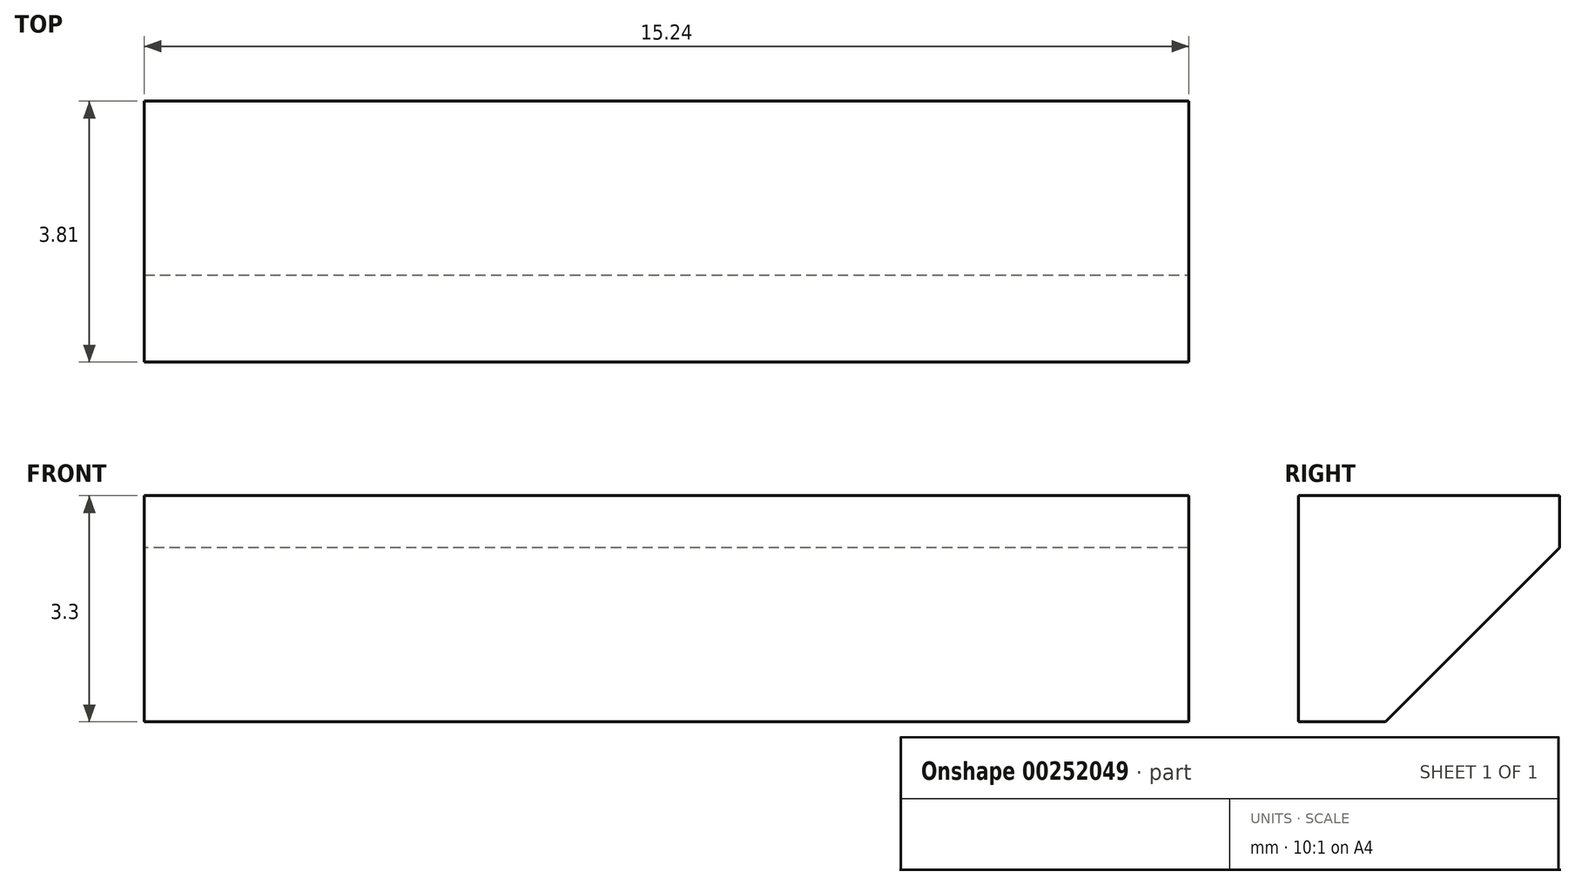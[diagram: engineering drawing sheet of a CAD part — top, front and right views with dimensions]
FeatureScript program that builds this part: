
annotation { "Feature Type Name" : "Feature", "Feature Type Description" : "" }
export const myFeature = defineFeature(function(context is Context, id is Id, definition is map)
    precondition{}
    {
        {
            var Q0;
            Q0=qCreatedBy(makeId("Front.planeOp"),FACE);
            var sketch = newSketch(context, id + "F0", { "sketchPlane" : qUnion([Q0])});
            skLineSegment(sketch, "E0.bottom", {"start": v(-7.62, 1.65) * mm, "end": v(7.62, 1.65) * mm});
            skLineSegment(sketch, "E0.top", {"start": v(-7.62, -1.65) * mm, "end": v(7.62, -1.65) * mm});
            skLineSegment(sketch, "E0.left", {"start": v(-7.62, 1.65) * mm, "end": v(-7.62, -1.65) * mm});
            skLineSegment(sketch, "E0.right", {"start": v(7.62, 1.65) * mm, "end": v(7.62, -1.65) * mm});
            skPoint(sketch, "E0.middle", {"position": v(0, 0) * mm});
            skSolve(sketch);
        }
        {
            var Q0;
            Q0 = qSketchRegion(id + "F0", true);
            extrude(context, id + "F1", {"entities" : qUnion([Q0]), "depth" : 3.8 * mm});
        }
        {
            var Q0;
            Q0=makeQuery(id+"F1.opExtrude","CAP_EDGE",EDGE,{"disambiguationData":[OSD([sQuery(id+"F0.wireOp",EDGE,"E0.top")])],"isStart":true});
            chamfer(context, id + "F2", {"entities" : qUnion([Q0]), "width" : 2.54 * mm, "tangentPropagation" : true});
        }
    });
